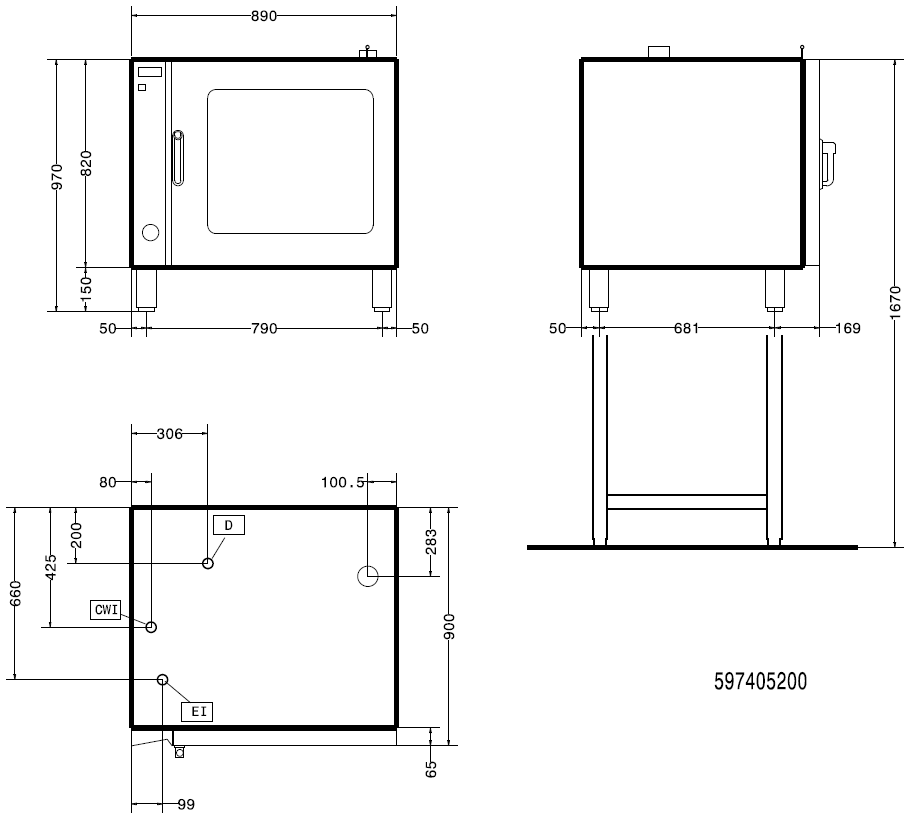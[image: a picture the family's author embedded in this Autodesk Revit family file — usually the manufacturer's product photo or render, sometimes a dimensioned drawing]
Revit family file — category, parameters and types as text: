
# Revit family: QF_ELECTROLUXPROFESSIONAL_240004_FCF10EOEM
name_source: partatom
category: Specialty Equipment
revit_build: Autodesk Revit 2018 (Build: 20190510_1515(x64)
units: mm (PartAtom-declared; Revit-internal decimal feet)

## family parameters
Always vertical = Yes
Cut with Voids When Loaded = No
Part Type = Normal
Room Calculation Point = No
Round Connector Dimension = Use Diameter
Shared = No
Work Plane-Based = No

## types (1)
- Standard
    Accessory = Yes
    Cold Water Size = 19 mm
    Compressed Air Pressure = 0.0 Pa
    Compressed Air Size = 0 mm
    Compressed Air Volume = 0.0 L/s
    Condensate Return Size = 0 mm
    Cycle = 50 Hz
    Depth Actual = 900 mm  [stored 2.95276 ft]
    Description = EL.CONV.OVEN 10GN1/1-SMART STEAM
    Direct Waste Size = 25 mm
    Gas Input Pressure = 0
    Gas KW = 0
    Gas Size = 0 mm
    HP = 23.2 HP
    Height Actual = 970 mm  [stored 3.18241 ft]
    Hot Water Size = 0 mm
    Item Number = 240004
    Length Actual = 890 mm  [stored 2.91995 ft]
    Manufacturer = Electrolux Professional
    Model = FCF10EOEM
    Phase = 3
    Refrigerant Compressor Remote = Yes
    Refrigeration Liquid Line Size = 0 mm
    Refrigeration Suction Line Size = 0 mm
    Steam Pounds per Hour = 0
    Steam Supply Maximum Pressure = 0.0 Pa
    Steam Supply Minimum Pressure = 0.0 Pa
    Steam Supply Size = 0 mm
    URL = http://professional.electrolux.com
    URL Manufacturer = http://professional.electrolux.com
    Volts = 380 V
    Watts = 0 W
    Weight = 121.20 kg

note: source unit labels omitted for Gas Input Pressure — the stored unit's dimension contradicts the parameter name (converter mislabeling)

note: [stored X ft] marks values corroborated as IEEE doubles in the binary element streams (Revit-internal decimal feet)

## geometry (parser evidence)
native form markers: Sweep x3
no freeform markers — native parametric forms only
